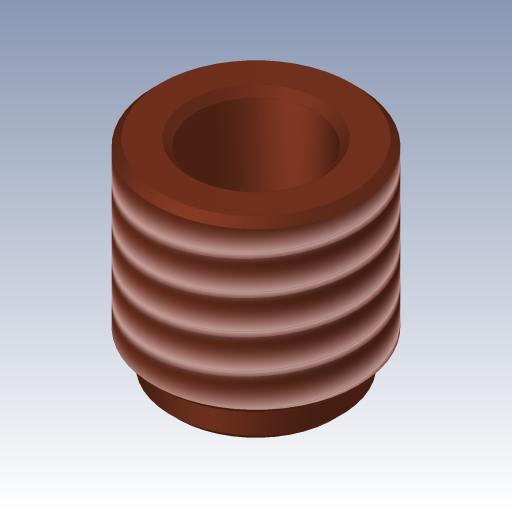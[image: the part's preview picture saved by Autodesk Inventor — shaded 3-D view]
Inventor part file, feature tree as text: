
AUTODESK INVENTOR PART (.ipt)
format: ipt  version: 2023.3 (Build 273359000, 359)  size: 259,584 bytes
history: native  units: in
note: dims shown in document units (in); Inventor stores cm internally (conversion verified against a paired STEP export)
features: revolve x1, chamfer x1, thread x1, sketch x1
ambient origin geometry x8: Origin, YZ Plane, XZ Plane, XY Plane, X Axis, Y Axis, Z Axis, Center Point
bodies: Body1 (feature_tree)
feature tree (4):
  revolve  "Umdrehung1"
  chamfer  "Fase1"  Distance=0.0591in
  thread  "Gewinde2"  [1 undecoded]
  sketch  "Skizze3"  dims[d4=0.0787in d5=0.0591in d6=0.1378in d8=0.1969in d9=0.2362in d10=0.0394in d11=0.2362in d12=90.0deg d13=0.0079in d14=0.0787in d15=45.0deg d18=0.1969in d19=0.0in]
note: 1 required parameter value undecoded (feature->parameter linkage not recoverable at this tier; creation-order binding heuristic only, values carry confidence <= 0.55)
